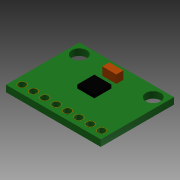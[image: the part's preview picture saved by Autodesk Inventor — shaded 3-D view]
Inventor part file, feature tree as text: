
AUTODESK INVENTOR PART (.ipt)
format: ipt  version: 2014 (Build 180170000, 170)  size: 167,936 bytes
history: native  units: in
note: dims shown in document units (in); Inventor stores cm internally (conversion verified against a paired STEP export)
features: extrude x6, sketch x6, pattern_linear x1
ambient origin geometry x8: Origin, YZ Plane, XZ Plane, XY Plane, X Axis, Y Axis, Z Axis, Center Point
bodies: Solid1 (feature_tree)
feature tree (13):
  extrude  "Extrusion1"  Depth=0.644in
  extrude  "Extrusion2"  Depth=0.057in
  extrude  "Extrusion3"  Depth=0.026in
  extrude  "Extrusion4"  Depth=0.057in TaperAngle=0.0deg
  extrude  "Extrusion5"  Depth=0.0625in
  extrude  "Extrusion6"  Depth=0.0715in TaperAngle=0.0deg
  pattern_linear  "Rectangular Pattern1"  Spacing1=0.15in  [1 undecoded]
  sketch  "Sketch1"  dims[d0=0.833in d1=0.644in]
  sketch  "Sketch2"  dims[d2=0.057in d3=0.0in d4=0.026in]
  sketch  "Sketch3"  dims[d5=0.026in d6=0.026in]
  sketch  "Sketch4"  dims[d7=0.13in d8=0.057in d9=0.0in]
  sketch  "Sketch5"  dims[d10=0.124in d11=0.0625in]
  sketch  "Sketch6"  dims[d12=0.09in d13=0.0715in d14=0.0in d15=0.15in d16=0.15in d17=0.0565in d18=0.03in d19=0.0in d20=0.04in d21=0.04in d22=0.03in d23=0.0in d24=0.07in d25=0.001in d26=0.0in d27=3.1496in d29=0.1in]
note: 1 required parameter value undecoded (feature->parameter linkage not recoverable at this tier; creation-order binding heuristic only, values carry confidence <= 0.55)
